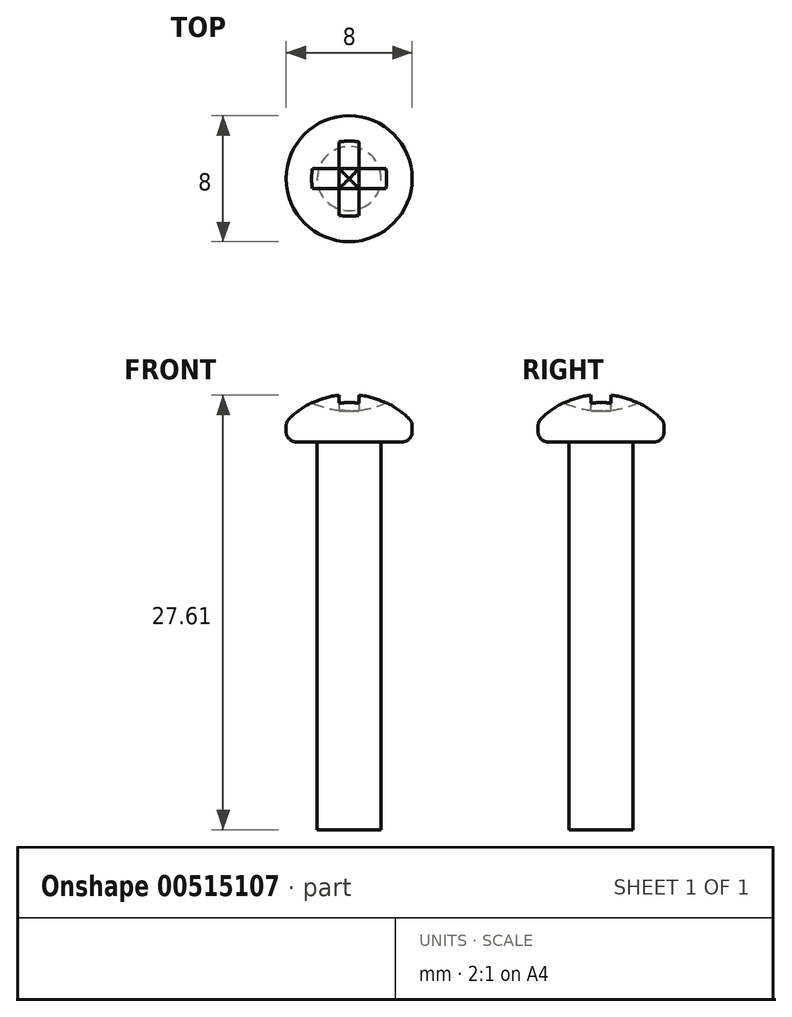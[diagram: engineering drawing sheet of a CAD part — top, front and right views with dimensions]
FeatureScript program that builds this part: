
annotation { "Feature Type Name" : "Feature", "Feature Type Description" : "" }
export const myFeature = defineFeature(function(context is Context, id is Id, definition is map)
    precondition{}
    {
        {
            var Q0;
            Q0=qCreatedBy(makeId("Front.planeOp"),FACE);
            var sketch = newSketch(context, id + "F0", { "sketchPlane" : qUnion([Q0])});
            skLineSegment(sketch, "E0", {"start": v(0, 0) * mm, "end": v(2.03, 0) * mm});
            skLineSegment(sketch, "E1", {"start": v(2.03, 0) * mm, "end": v(2.03, 24.64) * mm});
            skLineSegment(sketch, "E2", {"start": v(2.03, 24.64) * mm, "end": v(4, 24.64) * mm});
            skLineSegment(sketch, "E3", {"start": v(4, 24.64) * mm, "end": v(4, 25.9) * mm});
            skArc(sketch, "E4", {"start": v(4, 25.9) * mm, "mid": v(2.19, 27.22) * mm, "end": v(0, 27.69) * mm});
            skLineSegment(sketch, "E5", {"start": v(0, 27.69) * mm, "end": v(0, 0) * mm});
            skSolve(sketch);
        }
        {
            var Q0;
            Q0=makeQuery(id+"F0.imprint","IMPRINT",FACE,{"disambiguationData":[TD([[makeQuery(id+"F0.imprint","IMPRINT",EDGE,{"derivedFrom":sQuery(id+"F0.wireOp",EDGE,"E0")}),1.0]])]});
            var Q1;
            Q1=sQuery(id+"F0.wireOp",EDGE,"E5");
            revolve(context, id + "F1", {"entities" : qUnion([Q0]), "axis" : qUnion([Q1]), "revolveType" : RevolveType.FULL});
        }
        {
            var Q0;
            Q0=makeQuery(id+"F1.opRevolve","SWEPT_EDGE",EDGE,{"disambiguationData":[OSD([sQuery(id+"F0.wireOp",EDGE,"E2"),sQuery(id+"F0.wireOp",EDGE,"E3")])]});
            var Q1;
            Q1=makeQuery(id+"F1.opRevolve","SWEPT_EDGE",EDGE,{"disambiguationData":[OSD([sQuery(id+"F0.wireOp",EDGE,"E3"),sQuery(id+"F0.wireOp",EDGE,"E4")])]});
            fillet(context, id + "F2", {"entities" : qUnion([Q0, Q1]), "radius" : 0.64 * mm, "tangentPropagation" : true, "allowEdgeOverflow" : false});
        }
        {
            var Q0;
            Q0=qCreatedBy(makeId("Right.planeOp"),FACE);
            var sketch = newSketch(context, id + "F3", { "sketchPlane" : qUnion([Q0])});
            skArc(sketch, "E6", {"start": v(3.81, 26.1) * mm, "mid": v(0, 27.69) * mm, "end": v(-3.81, 26.1) * mm, "construction": true});
            skLineSegment(sketch, "E7", {"start": v(0, 27.69) * mm, "end": v(0, 32.33) * mm, "construction": true});
            skCircle(sketch, "E8", {"center": v(0, 32.33) * mm, "radius": 5.72 * mm});
            skLineSegment(sketch, "E9.0", {"start": v(-3.81, 26.1) * mm, "end": v(3.81, 26.1) * mm, "construction": true});
            skSolve(sketch);
        }
        {
            var Q0;
            Q0=makeQuery(id+"F3.imprint","IMPRINT",FACE,{"disambiguationData":[TD([[makeQuery(id+"F3.imprint","IMPRINT",EDGE,{"derivedFrom":sQuery(id+"F3.wireOp",EDGE,"E8")}),1.0]])]});
            extrude(context, id + "F4", {"entities" : qUnion([Q0]), "operationType" : NewBodyOperationType.REMOVE, "endBound" : BoundingType.SYMMETRIC, "oppositeDirection" : true, "depth" : 1.27 * mm, "offsetDistance" : 25.4 * mm});
        }
        {
            var Q0;
            Q0=qCreatedBy(makeId("Front.planeOp"),FACE);
            var sketch = newSketch(context, id + "F5", { "sketchPlane" : qUnion([Q0])});
            skArc(sketch, "E10", {"start": v(-0.64, 27.65) * mm, "mid": v(0, 16.9) * mm, "end": v(0.64, 27.65) * mm, "construction": true});
            skArc(sketch, "E11", {"start": v(0.64, 27.65) * mm, "mid": v(0, 27.69) * mm, "end": v(-0.64, 27.65) * mm, "construction": true});
            skLineSegment(sketch, "E12", {"start": v(0, 27.65) * mm, "end": v(0, 32.33) * mm, "construction": true});
            skPoint(sketch, "E12.startSnap0", {"position": v(0, 27.69) * mm});
            skPoint(sketch, "E12.endSnap0", {"position": v(0, 27.69) * mm});
            skCircle(sketch, "E13", {"center": v(0, 32.33) * mm, "radius": 5.72 * mm});
            skLineSegment(sketch, "E14.0", {"start": v(-3.81, 26.1) * mm, "end": v(3.81, 26.1) * mm, "construction": true});
            skSolve(sketch);
        }
        {
            var Q0;
            Q0=makeQuery(id+"F5.imprint","IMPRINT",FACE,{"disambiguationData":[TD([[makeQuery(id+"F5.imprint","IMPRINT",EDGE,{"derivedFrom":sQuery(id+"F5.wireOp",EDGE,"E13")}),1.0]])]});
            extrude(context, id + "F6", {"entities" : qUnion([Q0]), "operationType" : NewBodyOperationType.REMOVE, "endBound" : BoundingType.SYMMETRIC, "depth" : 1.27 * mm, "offsetDistance" : 25.4 * mm});
        }
    });
